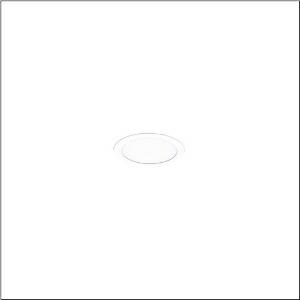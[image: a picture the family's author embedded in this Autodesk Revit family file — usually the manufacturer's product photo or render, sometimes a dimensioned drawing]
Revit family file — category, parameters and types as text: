
# Revit family: lunis_21_s_51db16ea91c
name_source: partatom
category: Lighting Fixtures
units: mm (PartAtom-declared; Revit-internal decimal feet)

## family parameters
Cut with Voids When Loaded = No
Host = Face
Light Source = No
Part Type = Normal
Room Calculation Point = No
Round Connector Dimension = Use Diameter
Shared = No

## types (1)
- --- (1 x LED, 1000 lm, 8 W, 6500K)
    Apparent Load = 8 VA
    CIE Flux Codes = 50 80 96 100 100
    Color Rendering = 80
    Color Temperature = 6500K
    Default Elevation = 1800 mm
    Description = Lunis 21,  S, downlight, light control with lens, of PMMA, optical cover: cover panel, of PC, opal, light emission: direct distribution, LED rated luminous flux: 770lm, light colour: 830/840/865, with terminal, 5-pole, mains connection: 220..240V, AC, 50..60Hz, housing, round, of diecast aluminium, traffic white (RAL 9016), diameter: 84mm, clamping range: 1..40mm, protection rating (complete): IP20, protection rating (on room side): IP54, insulation class (complete): insulation class II (safety insulation), certification: CE, impact resistance: IK03, packaging unit: 1 piece
    Height = 0 mm  [stored 0 ft]
    Lamp = 1 x LED
    Lamp Light Flux = 1000 lm
    Lamp Power = 8 W
    Lamp count = 1
    Length = 84 mm
    Luminous efficacy = 125 lm/W
    Manufacturer = Siteco
    ModVariant = No
    Model = 51DB16EA91C
    Mounting Place = Ceiling
    Mounting Type = Recessed
    Number of Poles = 1
    OnlyDefault = Yes
    Power Factor = 1
    Product Name = Lunis 21 S
    Product group = downlight
    ProductGroupID = 401
    Protection Class = Protection class II
    Protection Degree = IP 20
    RLX_Detail_Level = 1
    RLX_Emergency_Light_Flux = 0 lm
    RLX_Emergency_Type = 0
    RLX_Emergency_Type_DB = No
    RlxData = <blob elided: 8725 chars, md5=dab4adc0>
    Socket = socket
    Standby Power = 0 W
    System Light Flux = 1000 lm
    System Power = 8 W
    Type Comments = individual setting: colour temperature 6500K, luminous flux: 100 % | (OFF | OFF | ON | OFF) | 200 mA
    Type Image = l_1290838.jpg
    URL = http://relux.com
    VarID = @adj_038591
    Voltage = 0 V
    Weight = 0.00 kg
    Width = 0 mm  [stored 0 ft]

note: [stored X ft] marks values corroborated as IEEE doubles in the binary element streams (Revit-internal decimal feet)

## geometry (parser evidence)
native form markers: Sweep x9
no freeform markers — native parametric forms only
